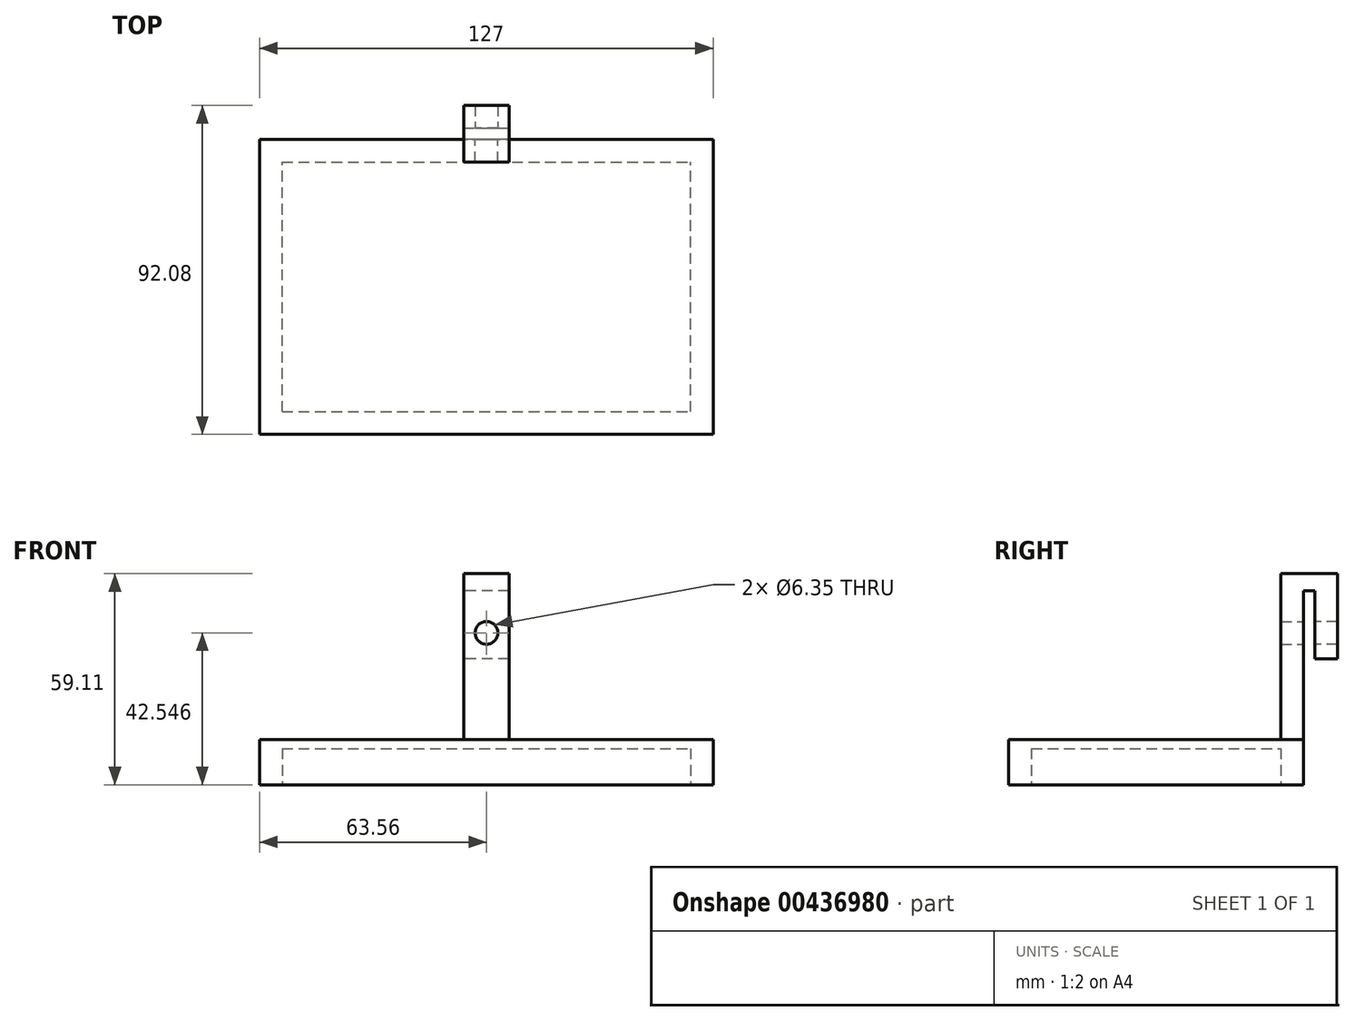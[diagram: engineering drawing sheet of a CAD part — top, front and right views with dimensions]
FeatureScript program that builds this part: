
annotation { "Feature Type Name" : "Feature", "Feature Type Description" : "" }
export const myFeature = defineFeature(function(context is Context, id is Id, definition is map)
    precondition{}
    {
        {
            var Q0;
            Q0=qCreatedBy(makeId("Front.planeOp"),FACE);
            var sketch = newSketch(context, id + "F0", { "sketchPlane" : qUnion([Q0])});
            skLineSegment(sketch, "E0", {"start": v(0, 27.04) * mm, "end": v(6.29, 27.04) * mm});
            skLineSegment(sketch, "E1", {"start": v(0, 27.04) * mm, "end": v(-6.41, 27.04) * mm});
            skLineSegment(sketch, "E2", {"start": v(6.29, 27.04) * mm, "end": v(6.29, -14.61) * mm});
            skLineSegment(sketch, "E3", {"start": v(6.29, -27.31) * mm, "end": v(-6.41, -27.31) * mm});
            skLineSegment(sketch, "E4", {"start": v(-6.41, -14.61) * mm, "end": v(-6.41, 27.04) * mm});
            skLineSegment(sketch, "E5", {"start": v(-6.41, 27.04) * mm, "end": v(-6.41, 31.8) * mm});
            skLineSegment(sketch, "E6", {"start": v(-6.41, 31.8) * mm, "end": v(6.29, 31.8) * mm});
            skLineSegment(sketch, "E7", {"start": v(6.29, 31.8) * mm, "end": v(6.29, 27.04) * mm});
            skCircle(sketch, "E8", {"center": v(0, 15.24) * mm, "radius": 3.18 * mm});
            skLineSegment(sketch, "E9", {"start": v(-6.41, -14.61) * mm, "end": v(-63.56, -14.61) * mm});
            skLineSegment(sketch, "E10", {"start": v(-63.56, -14.61) * mm, "end": v(-63.56, -27.31) * mm});
            skLineSegment(sketch, "E11", {"start": v(-63.56, -27.31) * mm, "end": v(-6.41, -27.31) * mm});
            skLineSegment(sketch, "E12.bottom", {"start": v(6.29, -27.31) * mm, "end": v(63.44, -27.31) * mm});
            skLineSegment(sketch, "E12.top", {"start": v(6.29, -14.61) * mm, "end": v(63.44, -14.61) * mm});
            skLineSegment(sketch, "E12.right", {"start": v(63.44, -27.31) * mm, "end": v(63.44, -14.61) * mm});
            skSolve(sketch);
        }
        {
            var Q0;
            Q0=makeQuery(id+"F0.imprint","IMPRINT",FACE,{"disambiguationData":[TD([[makeQuery(id+"F0.imprint","IMPRINT",EDGE,{"derivedFrom":sQuery(id+"F0.wireOp",EDGE,"E0")}),-1.0]])]});
            extrude(context, id + "F1", {"entities" : qUnion([Q0]), "depth" : 6.35 * mm});
        }
        {
            var Q0;
            Q0=makeQuery(id+"F0.imprint","IMPRINT",FACE,{"disambiguationData":[TD([[makeQuery(id+"F0.imprint","IMPRINT",EDGE,{"derivedFrom":sQuery(id+"F0.wireOp",EDGE,"E0")}),1.0]])]});
            extrude(context, id + "F2", {"entities" : qUnion([Q0]), "operationType" : NewBodyOperationType.ADD, "depth" : 6.35 * mm});
        }
        {
            var Q0;
            Q0=makeQuery(id+"F0.imprint","IMPRINT",FACE,{"disambiguationData":[TD([[makeQuery(id+"F0.imprint","IMPRINT",EDGE,{"derivedFrom":sQuery(id+"F0.wireOp",EDGE,"E0")}),1.0]])]});
            extrude(context, id + "F3", {"entities" : qUnion([Q0]), "operationType" : NewBodyOperationType.ADD, "oppositeDirection" : true, "depth" : 9.52 * mm});
        }
        {
            var Q0;
            Q0=makeQuery(id+"F3.opExtrude","SWEPT_FACE",FACE,{"disambiguationData":[OSD([sQuery(id+"F0.wireOp",EDGE,"E0"),sQuery(id+"F0.wireOp",EDGE,"E1")])]});
            var sketch = newSketch(context, id + "F4", { "sketchPlane" : qUnion([Q0])});
            skLineSegment(sketch, "E13.bottom", {"start": v(-6.41, -3.17) * mm, "end": v(6.29, -3.17) * mm});
            skLineSegment(sketch, "E13.top", {"start": v(-6.41, -9.53) * mm, "end": v(6.29, -9.53) * mm});
            skLineSegment(sketch, "E13.right", {"start": v(6.29, -3.17) * mm, "end": v(6.29, -9.53) * mm});
            skSolve(sketch);
        }
        {
            var Q0;
            {var subQ0=sQuery(id+"F4.wireOp",EDGE,"E13.bottom");Q0=makeQuery(id+"F4.imprint","IMPRINT",FACE,{"disambiguationData":[TD([[makeQuery(id+"F4.imprint","IMPRINT",EDGE,{"derivedFrom":subQ0}),-1.0]])]});}
            extrude(context, id + "F5", {"entities" : qUnion([Q0]), "operationType" : NewBodyOperationType.ADD, "depth" : 19.05 * mm});
        }
        {
            var Q0;
            Q0=makeQuery(id+"F0.imprint","IMPRINT",FACE,{"disambiguationData":[TD([[makeQuery(id+"F0.imprint","IMPRINT",EDGE,{"derivedFrom":sQuery(id+"F0.wireOp",EDGE,"E8")}),1.0]])]});
            var Q1;
            Q1=sQuery(id+"F0.wireOp",EDGE,"E8");
            extrude(context, id + "F6", {"entities" : qUnion([Q0]), "operationType" : NewBodyOperationType.REMOVE, "surfaceEntities" : qUnion([Q1]), "oppositeDirection" : true, "depth" : 25.4 * mm});
        }
        {
            var Q0;
            {var subQ0=sQuery(id+"F0.wireOp",EDGE,"E1");var subQ1=sQuery(id+"F0.wireOp",EDGE,"E0");Q0=makeQuery(id+"F2.boolean.opBoolean","MERGE",FACE,{"derivedFrom":[makeQuery(id+"F1.opExtrude","CAP_FACE",FACE,{"disambiguationData":[OSD([subQ1,subQ0,sQuery(id+"F0.wireOp",EDGE,"E2"),sQuery(id+"F0.wireOp",EDGE,"E3"),sQuery(id+"F0.wireOp",EDGE,"E4"),sQuery(id+"F0.wireOp",EDGE,"E8"),sQuery(id+"F0.wireOp",EDGE,"E9"),sQuery(id+"F0.wireOp",EDGE,"E10"),sQuery(id+"F0.wireOp",EDGE,"E11"),sQuery(id+"F0.wireOp",EDGE,"E12.bottom"),sQuery(id+"F0.wireOp",EDGE,"E12.top"),sQuery(id+"F0.wireOp",EDGE,"E12.right")])],"isStart":false}),makeQuery(id+"F2.opExtrude","CAP_FACE",FACE,{"disambiguationData":[OSD([subQ1,subQ0,sQuery(id+"F0.wireOp",EDGE,"E5"),sQuery(id+"F0.wireOp",EDGE,"E6"),sQuery(id+"F0.wireOp",EDGE,"E7")])],"isStart":false})]});}
            var sketch = newSketch(context, id + "F7", { "sketchPlane" : qUnion([Q0])});
            skLineSegment(sketch, "E14.bottom", {"start": v(-63.56, -14.61) * mm, "end": v(63.44, -14.61) * mm});
            skLineSegment(sketch, "E14.top", {"start": v(-63.56, -27.31) * mm, "end": v(63.44, -27.31) * mm});
            skLineSegment(sketch, "E14.left", {"start": v(-63.56, -14.61) * mm, "end": v(-63.56, -27.31) * mm});
            skLineSegment(sketch, "E14.right", {"start": v(63.44, -14.61) * mm, "end": v(63.44, -27.31) * mm});
            skSolve(sketch);
        }
        {
            var Q0;
            Q0 = qSketchRegion(id + "F7", true);
            extrude(context, id + "F8", {"entities" : qUnion([Q0]), "operationType" : NewBodyOperationType.ADD, "depth" : 76.2 * mm});
        }
        {
            var Q0;
            Q0=makeQuery(id+"F8.boolean.opBoolean","MERGE",FACE,{"derivedFrom":[makeQuery(id+"F1.opExtrude","SWEPT_FACE",FACE,{"disambiguationData":[OSD([sQuery(id+"F0.wireOp",EDGE,"E3"),sQuery(id+"F0.wireOp",EDGE,"E11"),sQuery(id+"F0.wireOp",EDGE,"E12.bottom")])]}),makeQuery(id+"F8.opExtrude","SWEPT_FACE",FACE,{"disambiguationData":[OSD([sQuery(id+"F7.wireOp",EDGE,"E14.top")])]})]});
            var sketch = newSketch(context, id + "F9", { "sketchPlane" : qUnion([Q0])});
            skLineSegment(sketch, "E15.bottom", {"start": v(-63.56, 82.55) * mm, "end": v(-57.21, 82.55) * mm});
            skLineSegment(sketch, "E15.top", {"start": v(-63.56, 76.2) * mm, "end": v(-57.21, 76.2) * mm});
            skLineSegment(sketch, "E15.left", {"start": v(-63.56, 82.55) * mm, "end": v(-63.56, 76.2) * mm});
            skLineSegment(sketch, "E15.right", {"start": v(-57.21, 82.55) * mm, "end": v(-57.21, 76.2) * mm});
            skLineSegment(sketch, "E16.bottom", {"start": v(57.09, 6.35) * mm, "end": v(63.44, 6.35) * mm});
            skLineSegment(sketch, "E16.top", {"start": v(57.09, 0) * mm, "end": v(63.44, 0) * mm});
            skLineSegment(sketch, "E16.left", {"start": v(57.09, 6.35) * mm, "end": v(57.09, 0) * mm});
            skLineSegment(sketch, "E16.right", {"start": v(63.44, 6.35) * mm, "end": v(63.44, 0) * mm});
            skLineSegment(sketch, "E17.bottom", {"start": v(-57.21, 76.2) * mm, "end": v(57.09, 76.2) * mm});
            skLineSegment(sketch, "E17.top", {"start": v(-57.21, 6.35) * mm, "end": v(57.09, 6.35) * mm});
            skLineSegment(sketch, "E17.left", {"start": v(-57.21, 76.2) * mm, "end": v(-57.21, 6.35) * mm});
            skLineSegment(sketch, "E17.right", {"start": v(57.09, 76.2) * mm, "end": v(57.09, 6.35) * mm});
            skSolve(sketch);
        }
        {
            var Q0;
            Q0=makeQuery(id+"F9.imprint","IMPRINT",FACE,{"disambiguationData":[TD([[makeQuery(id+"F9.imprint","IMPRINT",EDGE,{"derivedFrom":sQuery(id+"F9.wireOp",EDGE,"E17.bottom")}),-1.0]])]});
            extrude(context, id + "F10", {"entities" : qUnion([Q0]), "operationType" : NewBodyOperationType.REMOVE, "oppositeDirection" : true, "depth" : 10.16 * mm});
        }
    });
